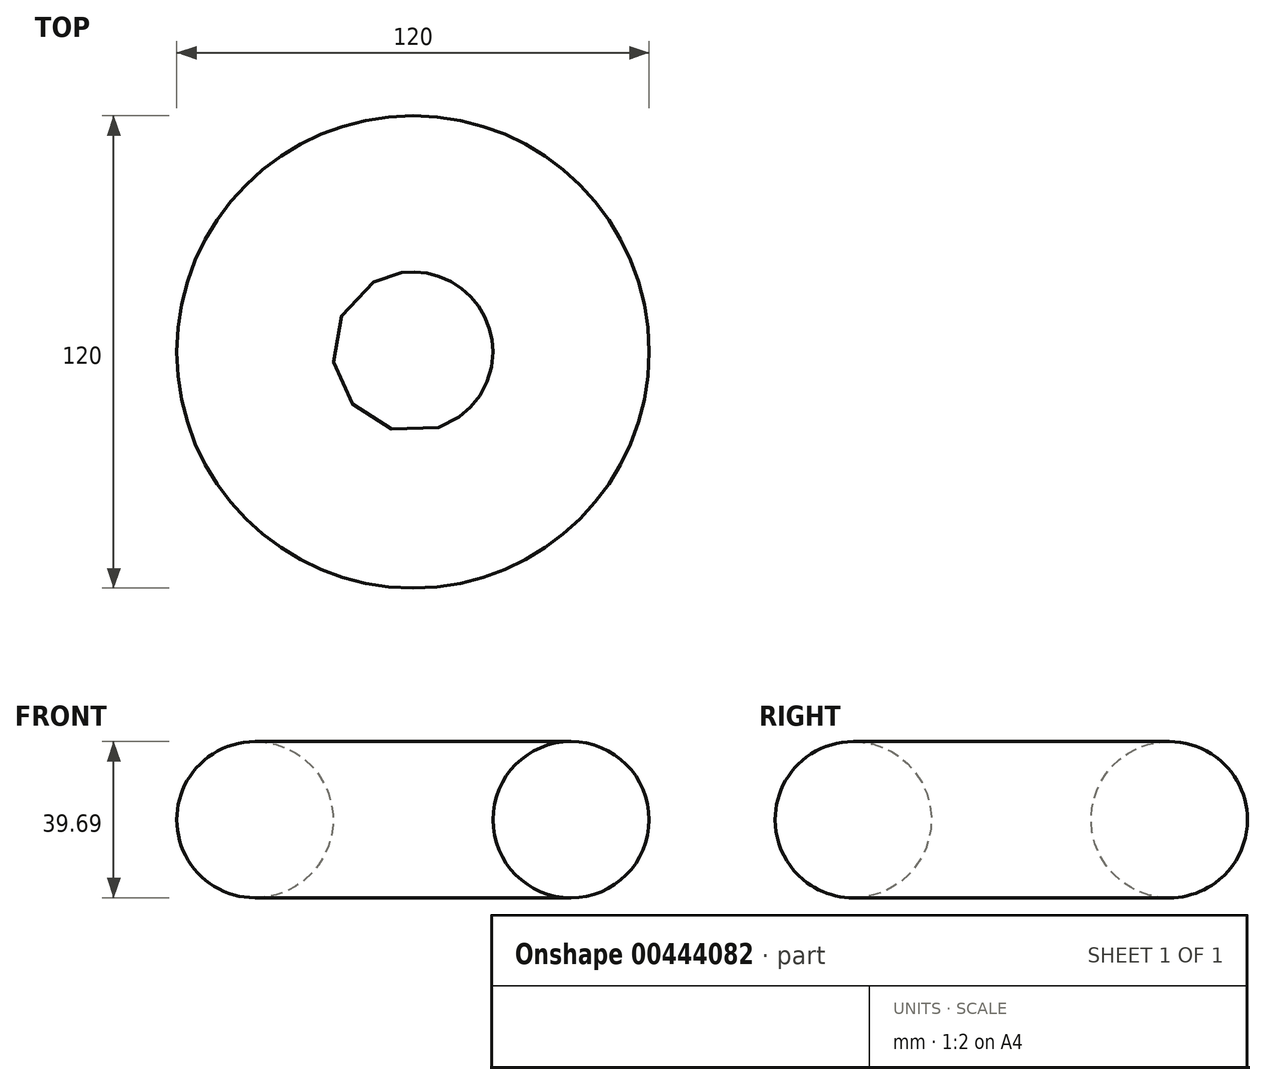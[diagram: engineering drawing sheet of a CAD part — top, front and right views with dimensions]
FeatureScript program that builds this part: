
annotation { "Feature Type Name" : "Feature", "Feature Type Description" : "" }
export const myFeature = defineFeature(function(context is Context, id is Id, definition is map)
    precondition{}
    {
        {
            var Q0;
            Q0=qCreatedBy(makeId("Right.planeOp"),FACE);
            var sketch = newSketch(context, id + "F0", { "sketchPlane" : qUnion([Q0])});
            skLineSegment(sketch, "E0", {"start": v(0, 0) * mm, "end": v(0, 38.45) * mm, "construction": true});
            skSolve(sketch);
        }
        {
            var Q0;
            Q0=qCreatedBy(makeId("Front.planeOp"),FACE);
            var sketch = newSketch(context, id + "F1", { "sketchPlane" : qUnion([Q0])});
            skCircle(sketch, "E1", {"center": v(-40.15, 33.07) * mm, "radius": 19.85 * mm});
            skCircle(sketch, "E2", {"center": v(-40.15, 33.07) * mm, "radius": 20.6 * mm});
            skSolve(sketch);
        }
        {
            var Q0;
            Q0=makeQuery(id+"F1.imprint","IMPRINT",FACE,{"disambiguationData":[TD([[makeQuery(id+"F1.imprint","IMPRINT",EDGE,{"derivedFrom":sQuery(id+"F1.wireOp",EDGE,"E1")}),1.0]])]});
            var Q1;
            Q1=sQuery(id+"F1.wireOp",EDGE,"E1");
            var Q2;
            Q2=sQuery(id+"F0.wireOp",EDGE,"E0");
            revolve(context, id + "F2", {"bodyType" : ToolBodyType.SURFACE, "entities" : qUnion([Q0]), "surfaceEntities" : qUnion([Q1]), "axis" : qUnion([Q2]), "revolveType" : RevolveType.FULL});
        }
    });
